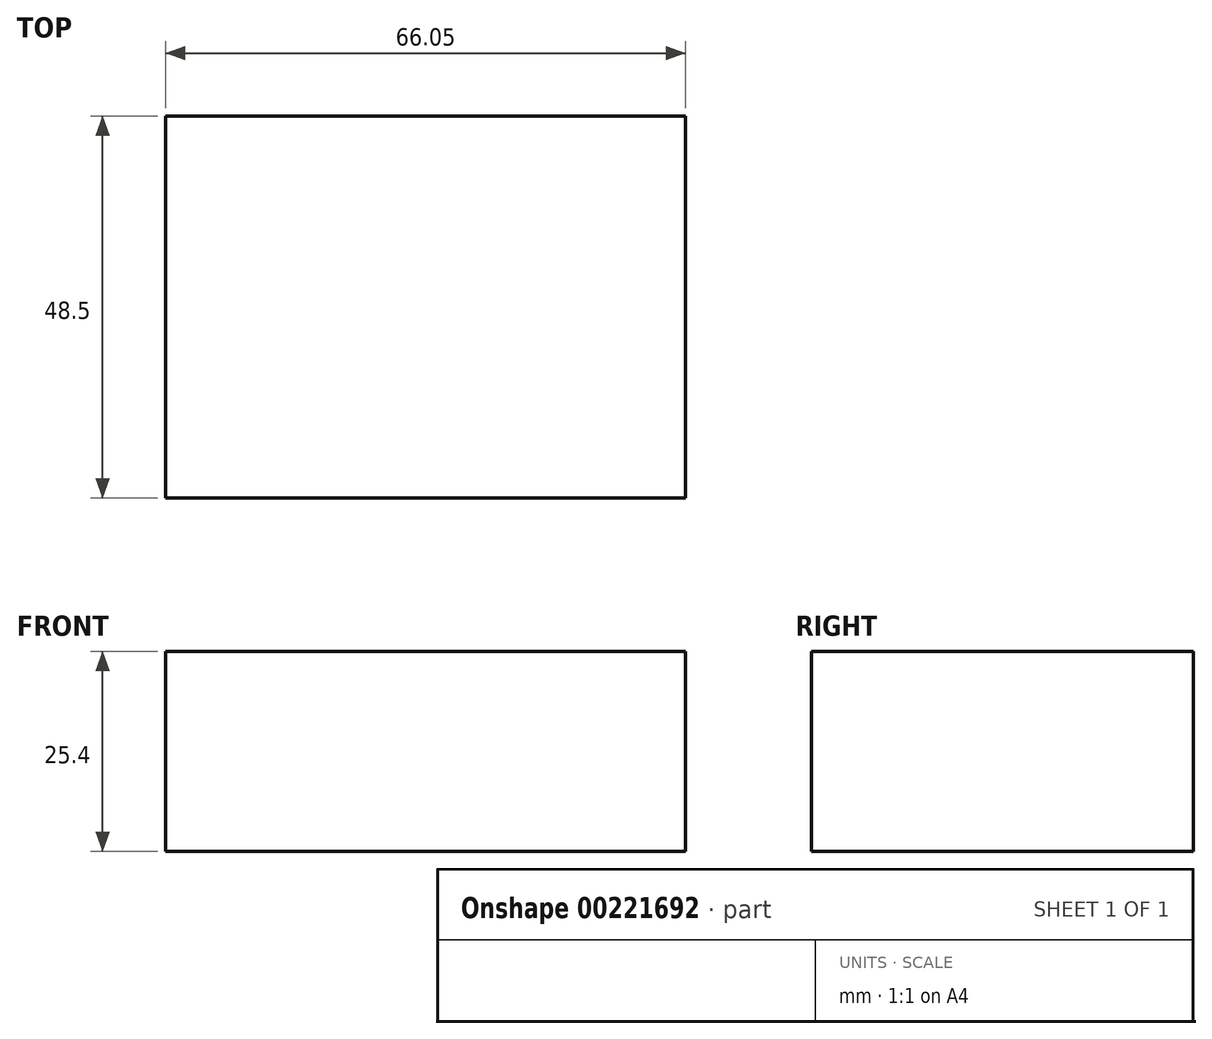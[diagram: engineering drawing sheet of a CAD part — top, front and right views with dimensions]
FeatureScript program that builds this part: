
annotation { "Feature Type Name" : "Feature", "Feature Type Description" : "" }
export const myFeature = defineFeature(function(context is Context, id is Id, definition is map)
    precondition{}
    {
        {
            var Q0;
            Q0=qCreatedBy(makeId("Top.planeOp"),FACE);
            var sketch = newSketch(context, id + "F0", { "sketchPlane" : qUnion([Q0])});
            skLineSegment(sketch, "E0.bottom", {"start": v(-3.35, 5.93) * mm, "end": v(8.79, 5.93) * mm});
            skLineSegment(sketch, "E0.top", {"start": v(-3.35, -5.93) * mm, "end": v(2.84, -5.93) * mm});
            skLineSegment(sketch, "E0.left", {"start": v(-7.92, 1.36) * mm, "end": v(-7.92, -1.36) * mm});
            skLineSegment(sketch, "E0.right", {"start": v(8.79, 5.93) * mm, "end": v(8.79, -3.47) * mm});
            skPoint(sketch, "E1", {"position": v(-7.92, 0) * mm});
            skPoint(sketch, "E2.visualSharp", {"position": v(-7.92, 5.93) * mm});
            skArc(sketch, "E2.filletArc", {"start": v(-3.35, 5.93) * mm, "mid": v(-6.59, 4.6) * mm, "end": v(-7.92, 1.36) * mm});
            skPoint(sketch, "E3.visualSharp", {"position": v(-7.92, -5.93) * mm});
            skArc(sketch, "E3.filletArc", {"start": v(-7.92, -1.36) * mm, "mid": v(-6.59, -4.6) * mm, "end": v(-3.35, -5.93) * mm});
            skCircle(sketch, "E4", {"center": v(0, 0) * mm, "radius": 1.97 * mm});
            skLineSegment(sketch, "E5", {"start": v(2.84, -5.93) * mm, "end": v(2.84, -3.47) * mm});
            skLineSegment(sketch, "E6", {"start": v(2.84, -3.47) * mm, "end": v(8.79, -3.47) * mm});
            skSolve(sketch);
        }
        {
            var Q0;
            Q0=makeQuery(id+"F0.imprint","IMPRINT",FACE,{"disambiguationData":[TD([[makeQuery(id+"F0.imprint","IMPRINT",EDGE,{"derivedFrom":sQuery(id+"F0.wireOp",EDGE,"E0.bottom")}),-1.0]])]});
            extrude(context, id + "F1", {"entities" : qUnion([Q0]), "depth" : 3.45 * mm});
        }
        {
            var Q0;
            Q0=makeQuery(id+"F1.opExtrude","SWEPT_FACE",FACE,{"disambiguationData":[OSD([sQuery(id+"F0.wireOp",EDGE,"E0.right")])]});
            var sketch = newSketch(context, id + "F2", { "sketchPlane" : qUnion([Q0])});
            skLineSegment(sketch, "E7", {"start": v(-8.74, 2.5) * mm, "end": v(-4.23, 2.5) * mm});
            skLineSegment(sketch, "E8", {"start": v(-3.98, 2.76) * mm, "end": v(-3.98, 6.3) * mm});
            skLineSegment(sketch, "E9", {"start": v(-3.98, 6.3) * mm, "end": v(3.98, 6.3) * mm});
            skLineSegment(sketch, "E10", {"start": v(3.98, 6.3) * mm, "end": v(3.98, 2.76) * mm});
            skLineSegment(sketch, "E11", {"start": v(4.23, 2.5) * mm, "end": v(8.7, 2.5) * mm});
            skLineSegment(sketch, "E12", {"start": v(8.7, 2.5) * mm, "end": v(8.7, 8.8) * mm});
            skLineSegment(sketch, "E13", {"start": v(8.7, 8.8) * mm, "end": v(-8.92, 8.92) * mm});
            skLineSegment(sketch, "E14", {"start": v(-8.92, 8.92) * mm, "end": v(-8.74, 2.5) * mm});
            skPoint(sketch, "E15", {"position": v(0, 6.3) * mm});
            skPoint(sketch, "E16.visualSharp", {"position": v(-3.98, 2.5) * mm});
            skArc(sketch, "E16.filletArc", {"start": v(-4.23, 2.5) * mm, "mid": v(-4.05, 2.58) * mm, "end": v(-3.98, 2.76) * mm});
            skPoint(sketch, "E17.visualSharp", {"position": v(3.98, 2.5) * mm});
            skArc(sketch, "E17.filletArc", {"start": v(3.98, 2.76) * mm, "mid": v(4.05, 2.58) * mm, "end": v(4.23, 2.5) * mm});
            skSolve(sketch);
        }
        {
            var Q0;
            Q0 = qSketchRegion(id + "F2", true);
            extrude(context, id + "F3", {"entities" : qUnion([Q0]), "operationType" : NewBodyOperationType.REMOVE, "endBound" : BoundingType.SYMMETRIC, "oppositeDirection" : true, "depth" : 127 * mm});
        }
        {
            var Q0;
            Q0=makeQuery(id+"F1.opExtrude","SWEPT_FACE",FACE,{"disambiguationData":[OSD([sQuery(id+"F0.wireOp",EDGE,"E0.top")])]});
            var sketch = newSketch(context, id + "F4", { "sketchPlane" : qUnion([Q0])});
            skPoint(sketch, "E18", {"position": v(4.09, -1.63) * mm});
            skArc(sketch, "E19", {"start": v(8.79, 1.4) * mm, "mid": v(7.75, 2.6) * mm, "end": v(6.42, 3.45) * mm});
            skLineSegment(sketch, "E20", {"start": v(6.42, 3.45) * mm, "end": v(2.36, 3.45) * mm});
            skLineSegment(sketch, "E21", {"start": v(8.79, 1.4) * mm, "end": v(8.79, -1.3) * mm});
            skLineSegment(sketch, "E22", {"start": v(8.79, -1.3) * mm, "end": v(9.92, -1.23) * mm});
            skLineSegment(sketch, "E23", {"start": v(9.92, -1.23) * mm, "end": v(9.92, 5.52) * mm});
            skLineSegment(sketch, "E24", {"start": v(9.92, 5.52) * mm, "end": v(2.43, 4.37) * mm});
            skLineSegment(sketch, "E25", {"start": v(2.43, 4.37) * mm, "end": v(2.36, 3.45) * mm});
            skSolve(sketch);
        }
        {
            var Q0;
            Q0 = qSketchRegion(id + "F4", true);
            extrude(context, id + "F5", {"entities" : qUnion([Q0]), "operationType" : NewBodyOperationType.REMOVE, "endBound" : BoundingType.SYMMETRIC, "oppositeDirection" : true, "depth" : 25.4 * mm});
        }
        {
            var Q0;
            Q0=makeQuery(id+"F3.boolean.opBoolean","INTERSECT",EDGE,{"derivedFrom":[makeQuery(id+"F1.opExtrude","CAP_FACE",FACE,{"disambiguationData":[OSD([sQuery(id+"F0.wireOp",EDGE,"E0.bottom"),sQuery(id+"F0.wireOp",EDGE,"E0.top"),sQuery(id+"F0.wireOp",EDGE,"E0.left"),sQuery(id+"F0.wireOp",EDGE,"E0.right"),sQuery(id+"F0.wireOp",EDGE,"E2.filletArc"),sQuery(id+"F0.wireOp",EDGE,"E3.filletArc"),sQuery(id+"F0.wireOp",EDGE,"E4"),sQuery(id+"F0.wireOp",EDGE,"E5"),sQuery(id+"F0.wireOp",EDGE,"E6")])],"isStart":false}),makeQuery(id+"F3.opExtrude","SWEPT_FACE",FACE,{"disambiguationData":[OSD([sQuery(id+"F2.wireOp",EDGE,"E8")])]})]});
            var Q1;
            Q1=makeQuery(id+"F3.boolean.opBoolean","INTERSECT",EDGE,{"derivedFrom":[makeQuery(id+"F1.opExtrude","CAP_FACE",FACE,{"disambiguationData":[OSD([sQuery(id+"F0.wireOp",EDGE,"E0.bottom"),sQuery(id+"F0.wireOp",EDGE,"E0.top"),sQuery(id+"F0.wireOp",EDGE,"E0.left"),sQuery(id+"F0.wireOp",EDGE,"E0.right"),sQuery(id+"F0.wireOp",EDGE,"E2.filletArc"),sQuery(id+"F0.wireOp",EDGE,"E3.filletArc"),sQuery(id+"F0.wireOp",EDGE,"E4"),sQuery(id+"F0.wireOp",EDGE,"E5"),sQuery(id+"F0.wireOp",EDGE,"E6")])],"isStart":false}),makeQuery(id+"F3.opExtrude","SWEPT_FACE",FACE,{"disambiguationData":[OSD([sQuery(id+"F2.wireOp",EDGE,"E10")])]})]});
            fillet(context, id + "F6", {"entities" : qUnion([Q0, Q1]), "radius" : 0.25 * mm, "tangentPropagation" : true, "allowEdgeOverflow" : false});
        }
        {
            var Q0;
            Q0=qCreatedBy(makeId("Front.planeOp"),FACE);
            var sketch = newSketch(context, id + "F7", { "sketchPlane" : qUnion([Q0])});
            skLineSegment(sketch, "E26", {"start": v(-1.97, 0.66) * mm, "end": v(-3.49, -1.97) * mm});
            skLineSegment(sketch, "E27", {"start": v(-3.49, -1.97) * mm, "end": v(3.49, -1.97) * mm});
            skLineSegment(sketch, "E28", {"start": v(3.49, -1.97) * mm, "end": v(1.97, 0.66) * mm});
            skLineSegment(sketch, "E29", {"start": v(1.97, 0.66) * mm, "end": v(-1.97, 0.66) * mm});
            skLineSegment(sketch, "E30", {"start": v(-3.3, 0) * mm, "end": v(-5.84, 0) * mm});
            skLineSegment(sketch, "E31", {"start": v(-1.97, 4.02) * mm, "end": v(-1.97, 7.79) * mm});
            skLineSegment(sketch, "E32", {"start": v(1.97, 4.45) * mm, "end": v(1.97, 7.25) * mm});
            skLineSegment(sketch, "E33", {"start": v(0, 4.1) * mm, "end": v(0, -3.77) * mm});
            skPoint(sketch, "E33.endSnap0", {"position": v(0, 0.66) * mm});
            skSolve(sketch);
        }
        {
            var Q0;
            {var subQ0=sQuery(id+"F7.wireOp",EDGE,"E26");Q0=makeQuery(id+"F7.imprint","IMPRINT",FACE,{"disambiguationData":[TD([[makeQuery(id+"F7.imprint","IMPRINT",EDGE,{"derivedFrom":subQ0}),1.0]])]});}
            var Q1;
            Q1=sQuery(id+"F7.wireOp",EDGE,"E33");
            revolve(context, id + "F8", {"operationType" : NewBodyOperationType.REMOVE, "entities" : qUnion([Q0]), "axis" : qUnion([Q1]), "revolveType" : RevolveType.FULL, "oppositeDirection" : true});
        }
        {
            var Q0;
            Q0=makeQuery(id+"F1.opExtrude","CAP_FACE",FACE,{"disambiguationData":[OSD([sQuery(id+"F0.wireOp",EDGE,"E0.bottom"),sQuery(id+"F0.wireOp",EDGE,"E0.top"),sQuery(id+"F0.wireOp",EDGE,"E0.left"),sQuery(id+"F0.wireOp",EDGE,"E0.right"),sQuery(id+"F0.wireOp",EDGE,"E2.filletArc"),sQuery(id+"F0.wireOp",EDGE,"E3.filletArc"),sQuery(id+"F0.wireOp",EDGE,"E4"),sQuery(id+"F0.wireOp",EDGE,"E5"),sQuery(id+"F0.wireOp",EDGE,"E6")])],"isStart":true});
            var sketch = newSketch(context, id + "F9", { "sketchPlane" : qUnion([Q0])});
            skCircle(sketch, "E34", {"center": v(0, 0) * mm, "radius": 2.2 * mm});
            skSolve(sketch);
        }
        {
            var Q0;
            Q0 = qSketchRegion(id + "F9", true);
            extrude(context, id + "F10", {"entities" : qUnion([Q0]), "operationType" : NewBodyOperationType.ADD, "oppositeDirection" : true, "depth" : 3.33 * mm, "hasSecondDirection" : true, "secondDirectionOppositeDirection" : true, "secondDirectionDepth" : 0.13 * mm});
        }
        {
            var Q0;
            Q0=qCreatedBy(makeId("Top.planeOp"),FACE);
            var sketch = newSketch(context, id + "F11", { "sketchPlane" : qUnion([Q0])});
            skLineSegment(sketch, "E35.bottom", {"start": v(-30.35, 24.17) * mm, "end": v(35.7, 24.17) * mm});
            skLineSegment(sketch, "E35.top", {"start": v(-30.35, -24.33) * mm, "end": v(35.7, -24.33) * mm});
            skLineSegment(sketch, "E35.left", {"start": v(-30.35, 24.17) * mm, "end": v(-30.35, -24.33) * mm});
            skLineSegment(sketch, "E35.right", {"start": v(35.7, 24.17) * mm, "end": v(35.7, -24.33) * mm});
            skSolve(sketch);
        }
        {
            var Q0;
            Q0 = qSketchRegion(id + "F11", true);
            extrude(context, id + "F12", {"entities" : qUnion([Q0]), "operationType" : NewBodyOperationType.ADD, "endBound" : BoundingType.SYMMETRIC, "depth" : 25.4 * mm});
        }
    });
